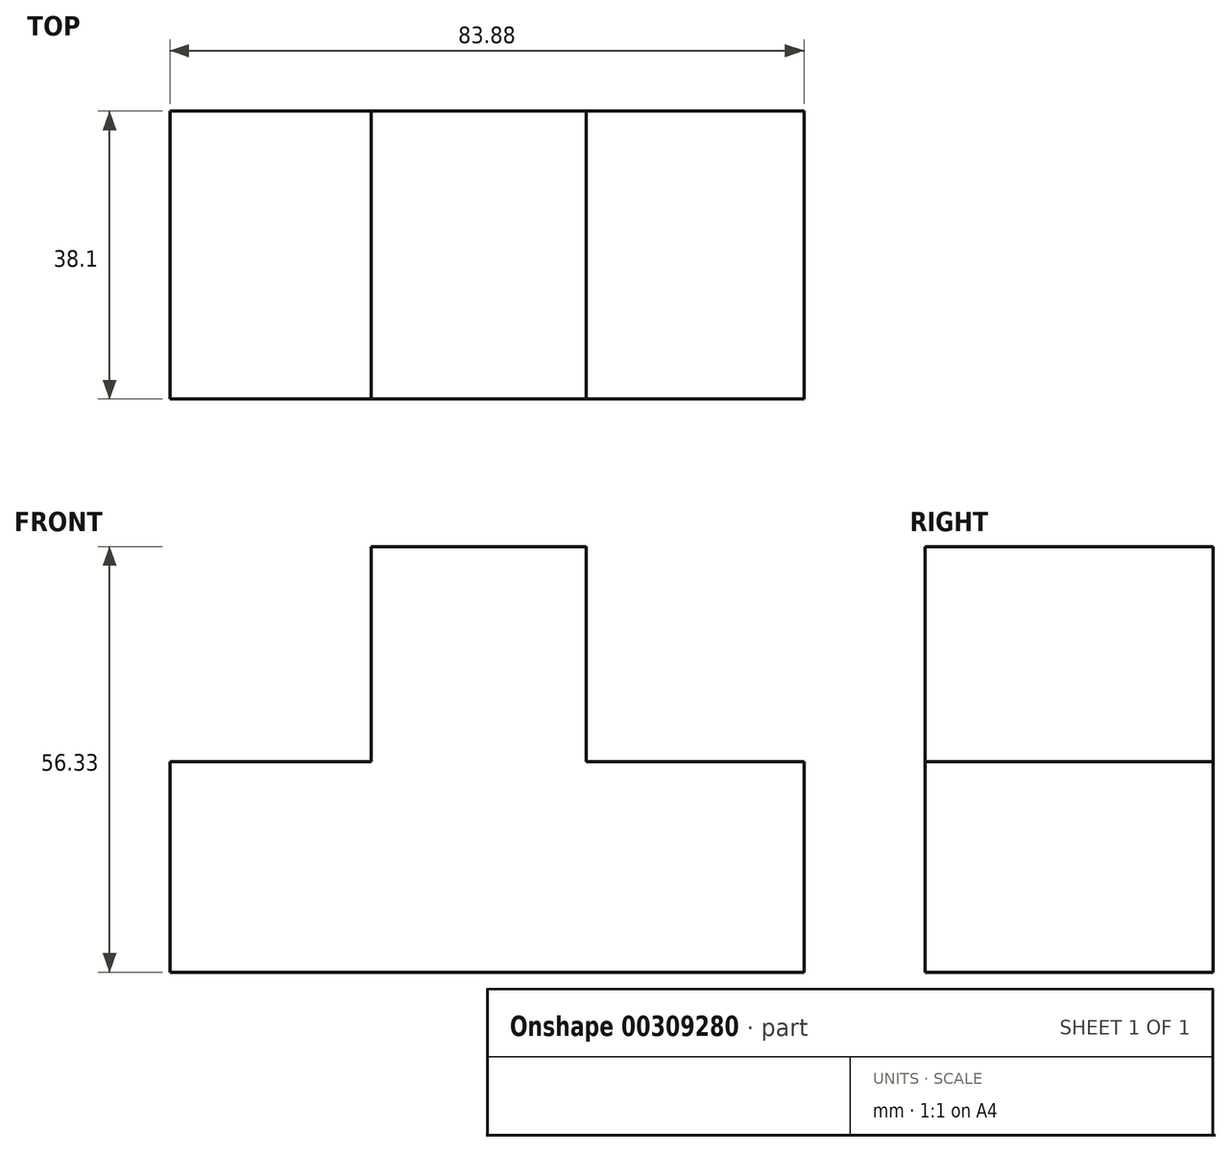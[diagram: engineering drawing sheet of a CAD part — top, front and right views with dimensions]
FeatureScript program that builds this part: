
annotation { "Feature Type Name" : "Feature", "Feature Type Description" : "" }
export const myFeature = defineFeature(function(context is Context, id is Id, definition is map)
    precondition{}
    {
        {
            var Q0;
            Q0=qCreatedBy(makeId("Front.planeOp"),FACE);
            var sketch = newSketch(context, id + "F0", { "sketchPlane" : qUnion([Q0])});
            skLineSegment(sketch, "E0", {"start": v(-44.26, -47.51) * mm, "end": v(39.62, -47.51) * mm});
            skLineSegment(sketch, "E1", {"start": v(39.62, -47.51) * mm, "end": v(39.62, -19.65) * mm});
            skLineSegment(sketch, "E2", {"start": v(39.62, -19.65) * mm, "end": v(10.83, -19.65) * mm});
            skLineSegment(sketch, "E3", {"start": v(10.83, -19.65) * mm, "end": v(10.83, 8.82) * mm});
            skLineSegment(sketch, "E4", {"start": v(10.83, 8.82) * mm, "end": v(-17.64, 8.82) * mm});
            skLineSegment(sketch, "E5", {"start": v(-17.64, 8.82) * mm, "end": v(-17.64, -19.65) * mm});
            skLineSegment(sketch, "E6", {"start": v(-17.64, -19.65) * mm, "end": v(-44.26, -19.65) * mm});
            skLineSegment(sketch, "E7", {"start": v(-44.26, -19.65) * mm, "end": v(-44.26, -47.51) * mm});
            skSolve(sketch);
        }
        {
            var Q0;
            Q0 = qSketchRegion(id + "F0", true);
            extrude(context, id + "F1", {"entities" : qUnion([Q0]), "depth" : 38.1 * mm});
        }
    });
